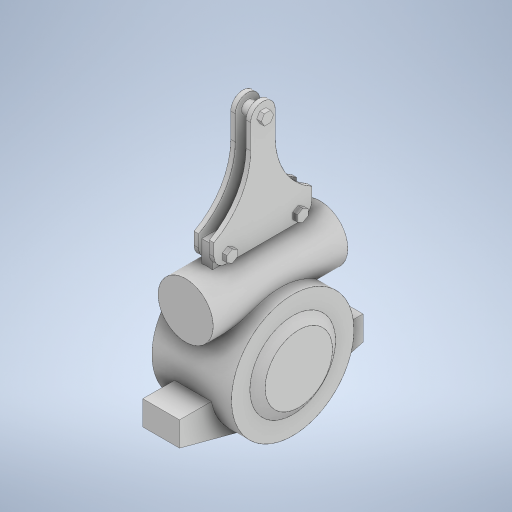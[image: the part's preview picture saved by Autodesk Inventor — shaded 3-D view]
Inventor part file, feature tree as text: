
AUTODESK INVENTOR PART (.ipt)
format: ipt  version: 2023 (Build 270158000, 158)  size: 443,392 bytes
history: native  units: in
note: dims shown in document units (in); Inventor stores cm internally (conversion verified against a paired STEP export)
features: extrude x6, sketch x6, revolve x1, mirror x1
ambient origin geometry x8: Origin, YZ Plane, XZ Plane, XY Plane, X Axis, Y Axis, Z Axis, Center Point
bodies: Solid1 (feature_tree)
feature tree (14):
  revolve  "Revolution1"  [1 undecoded]
  extrude  "Extrusion1"  TaperAngle=90.0deg  [1 undecoded]
  extrude  "Extrusion2"  Depth=2.75in
  extrude  "Extrusion3"  Depth=11.0in TaperAngle=0.0deg
  extrude  "Extrusion4"  Depth=1.0in
  extrude  "Extrusion5"  Depth=4.0in
  mirror  "Mirror1"
  extrude  "Extrusion6"  Depth=2.0in
  sketch  "Sketch1"  dims[d0=5.0in d1=6.5in]
  sketch  "Sketch2"  dims[d2=7.0in d3=90.0deg]
  sketch  "Sketch3"  dims[d4=1.5in d5=2.75in]
  sketch  "Sketch4"  dims[d6=4.5in d7=11.0in d8=0.0in]
  sketch  "Sketch5"  dims[d9=0.0in d10=1.0in]
  sketch  "Sketch7"  dims[d11=7.5in d12=4.0in d13=2.0in d14=3.0in d15=0.0in d16=2.0in d17=1.75in d18=2.0in d19=1.75in d20=0.875in d21=0.0in d22=0.0in d23=0.0in d24=0.2in d25=2.0in d26=7.0in d27=2.0in d28=9.0in d29=8.0in d30=0.375in d31=0.0in d32=1.0in d37=0.375in d38=0.0in d43=1.0in d44=1.0in d45=0.0in d46=0.875in d47=0.904in d48=0.875in d49=0.875in d50=0.875in]
note: 2 required parameter values undecoded (feature->parameter linkage not recoverable at this tier; creation-order binding heuristic only, values carry confidence <= 0.55)